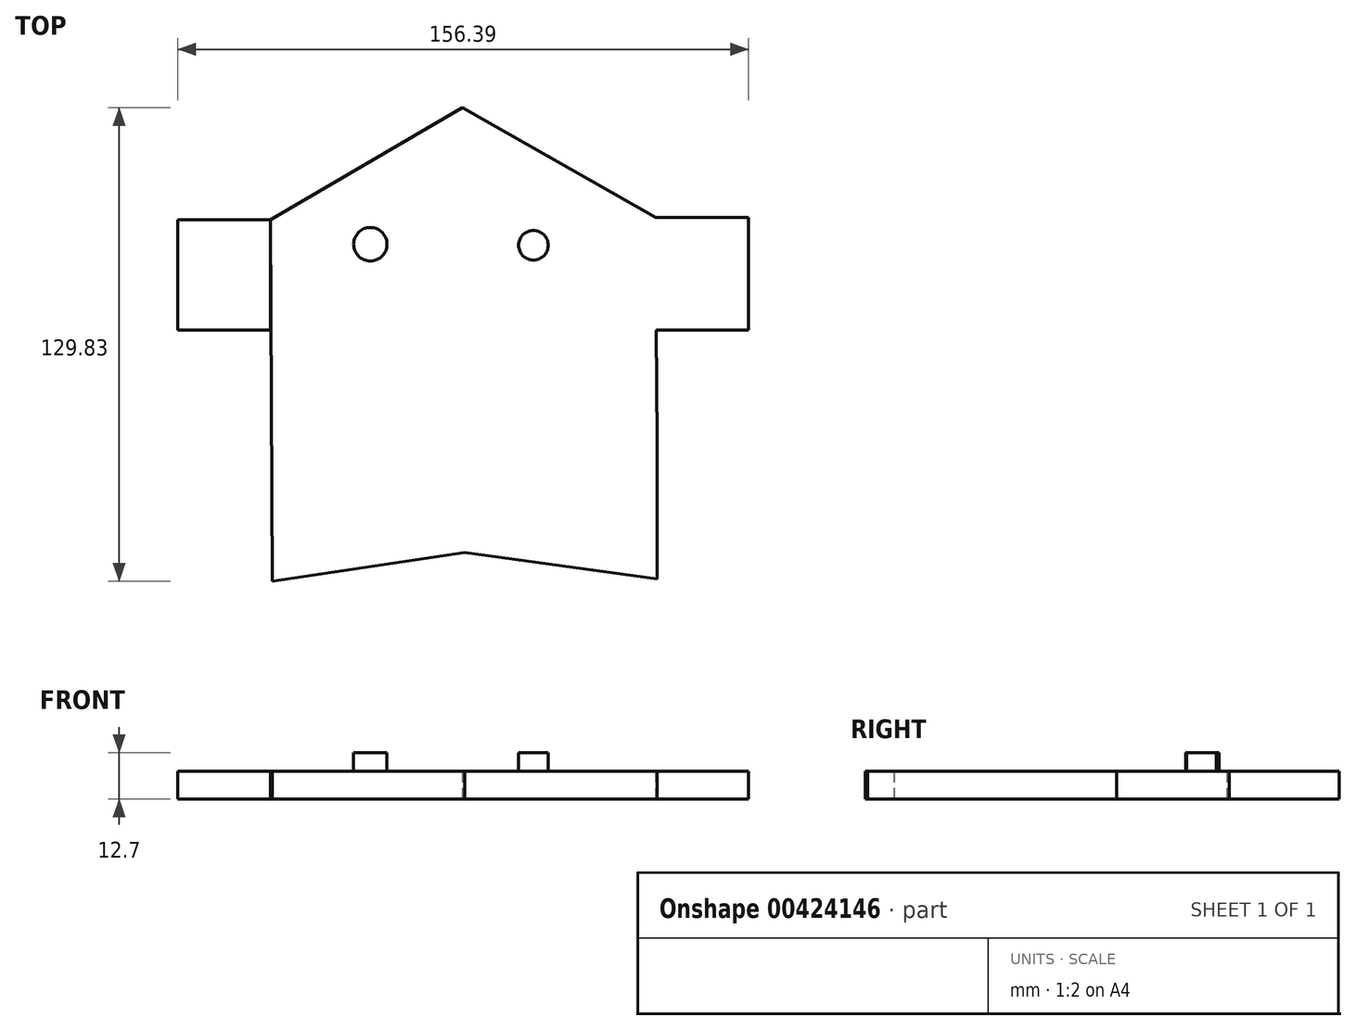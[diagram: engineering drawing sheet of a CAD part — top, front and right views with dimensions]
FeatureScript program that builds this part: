
annotation { "Feature Type Name" : "Feature", "Feature Type Description" : "" }
export const myFeature = defineFeature(function(context is Context, id is Id, definition is map)
    precondition{}
    {
        {
            var Q0;
            Q0=qCreatedBy(makeId("Top.planeOp"),FACE);
            var sketch = newSketch(context, id + "F0", { "sketchPlane" : qUnion([Q0])});
            skCircle(sketch, "E0.cCircle", {"center": v(0, 0) * mm, "radius": 52.8 * mm, "construction": true});
            skLineSegment(sketch, "E0.0", {"start": v(-52.96, 30.2) * mm, "end": v(-0.33, 60.96) * mm});
            skLineSegment(sketch, "E0.1", {"start": v(-0.33, 60.96) * mm, "end": v(52.63, 30.77) * mm});
            skLineSegment(sketch, "E0.2", {"start": v(52.63, 30.77) * mm, "end": v(52.96, -30.2) * mm});
            skLineSegment(sketch, "E0.3", {"start": v(52.96, -30.2) * mm, "end": v(0.33, -60.96) * mm});
            skLineSegment(sketch, "E0.4", {"start": v(0.33, -60.96) * mm, "end": v(-52.63, -30.77) * mm});
            skLineSegment(sketch, "E0.5", {"start": v(-52.63, -30.77) * mm, "end": v(-52.96, 30.2) * mm});
            skPoint(sketch, "E0.0.midPoint", {"position": v(-26.64, 45.58) * mm});
            skLineSegment(sketch, "E1", {"start": v(-52.63, -30.77) * mm, "end": v(-52.42, -68.87) * mm});
            skLineSegment(sketch, "E2", {"start": v(-52.42, -68.87) * mm, "end": v(0.33, -60.96) * mm});
            skLineSegment(sketch, "E3", {"start": v(52.96, -30.2) * mm, "end": v(52.96, -68.3) * mm});
            skLineSegment(sketch, "E4", {"start": v(52.96, -68.3) * mm, "end": v(0.33, -60.96) * mm});
            skLineSegment(sketch, "E5.bottom", {"start": v(-52.96, 30.2) * mm, "end": v(-78.36, 30.2) * mm});
            skLineSegment(sketch, "E5.top", {"start": v(-52.96, 0) * mm, "end": v(-78.36, 0) * mm});
            skLineSegment(sketch, "E5.left", {"start": v(-52.96, 30.2) * mm, "end": v(-52.96, 0) * mm});
            skLineSegment(sketch, "E5.right", {"start": v(-78.36, 30.2) * mm, "end": v(-78.36, 0) * mm});
            skLineSegment(sketch, "E6.bottom", {"start": v(52.63, 30.77) * mm, "end": v(78.03, 30.77) * mm});
            skLineSegment(sketch, "E6.top", {"start": v(52.63, 0) * mm, "end": v(78.03, 0) * mm});
            skLineSegment(sketch, "E6.left", {"start": v(52.63, 30.77) * mm, "end": v(52.63, 0) * mm});
            skLineSegment(sketch, "E6.right", {"start": v(78.03, 30.77) * mm, "end": v(78.03, 0) * mm});
            skSolve(sketch);
        }
        {
            var Q0;
            Q0=makeQuery(id+"F0.imprint","IMPRINT",FACE,{"disambiguationData":[TD([[makeQuery(id+"F0.imprint","IMPRINT",EDGE,{"derivedFrom":sQuery(id+"F0.wireOp",EDGE,"E0.3")}),1.0]])]});
            var Q1;
            {var subQ0=sQuery(id+"F0.wireOp",EDGE,"E6.bottom");Q1=makeQuery(id+"F0.imprint","IMPRINT",FACE,{"disambiguationData":[TD([[makeQuery(id+"F0.imprint","IMPRINT",EDGE,{"derivedFrom":subQ0}),-1.0]])]});}
            var Q2;
            Q2=makeQuery(id+"F0.imprint","IMPRINT",FACE,{"disambiguationData":[TD([[makeQuery(id+"F0.imprint","IMPRINT",EDGE,{"derivedFrom":sQuery(id+"F0.wireOp",EDGE,"E5.bottom")}),1.0]])]});
            var Q3;
            Q3=makeQuery(id+"F0.imprint","IMPRINT",FACE,{"disambiguationData":[TD([[makeQuery(id+"F0.imprint","IMPRINT",EDGE,{"derivedFrom":sQuery(id+"F0.wireOp",EDGE,"E0.4")}),1.0]])]});
            var Q4;
            Q4=makeQuery(id+"F0.imprint","IMPRINT",FACE,{"disambiguationData":[TD([[makeQuery(id+"F0.imprint","IMPRINT",EDGE,{"derivedFrom":sQuery(id+"F0.wireOp",EDGE,"E0.0")}),-1.0]])]});
            var Q5;
            {var subQ0=sQuery(id+"F0.wireOp",EDGE,"E6.left");Q5=makeQuery(id+"F0.imprint","IMPRINT",FACE,{"disambiguationData":[TD([[makeQuery(id+"F0.imprint","IMPRINT",EDGE,{"derivedFrom":subQ0}),1.0]])]});}
            extrude(context, id + "F1", {"entities" : qUnion([Q0, Q1, Q2, Q3, Q4, Q5]), "depth" : 7.62 * mm});
        }
        {
            var Q0;
            Q0=makeQuery(id+"F1.opExtrude","CAP_FACE",FACE,{"disambiguationData":[OSD([sQuery(id+"F0.wireOp",EDGE,"E0.0"),sQuery(id+"F0.wireOp",EDGE,"E0.1"),sQuery(id+"F0.wireOp",EDGE,"E0.2"),sQuery(id+"F0.wireOp",EDGE,"E0.5"),sQuery(id+"F0.wireOp",EDGE,"E1"),sQuery(id+"F0.wireOp",EDGE,"E2"),sQuery(id+"F0.wireOp",EDGE,"E3"),sQuery(id+"F0.wireOp",EDGE,"E4"),sQuery(id+"F0.wireOp",EDGE,"E6.bottom"),sQuery(id+"F0.wireOp",EDGE,"E6.top"),sQuery(id+"F0.wireOp",EDGE,"E6.right")])],"isStart":false});
            var sketch = newSketch(context, id + "F2", { "sketchPlane" : qUnion([Q0])});
            skCircle(sketch, "E7", {"center": v(-25.53, 23.71) * mm, "radius": 10.43 * mm});
            skCircle(sketch, "E8", {"center": v(18.85, 23.71) * mm, "radius": 10.43 * mm});
            skArc(sketch, "E9", {"start": v(-19.44, -6.97) * mm, "mid": v(-0.24, -17.82) * mm, "end": v(17.84, -5.2) * mm});
            skSolve(sketch);
        }
        {
            var Q0;
            Q0=sQuery(id+"F2.wireOp",EDGE,"E7");
            var Q1;
            Q1=sQuery(id+"F2.wireOp",EDGE,"E9");
            var Q2;
            Q2=sQuery(id+"F2.wireOp",EDGE,"E8");
            var Q3;
            Q3 = qConstructionFilter(qBodyType(qCreatedBy(id + "F6" ,EDGE), BodyType.WIRE), ConstructionObject.NO);
            extrude(context, id + "F3", {"bodyType" : ToolBodyType.SURFACE, "surfaceEntities" : qUnion([Q0, Q1, Q2, Q3]), "depth" : 5.08 * mm});
        }
        {
            var Q0;
            Q0=makeQuery(id+"F1.opExtrude","CAP_FACE",FACE,{"disambiguationData":[OSD([sQuery(id+"F0.wireOp",EDGE,"E0.0"),sQuery(id+"F0.wireOp",EDGE,"E0.1"),sQuery(id+"F0.wireOp",EDGE,"E0.2"),sQuery(id+"F0.wireOp",EDGE,"E0.5"),sQuery(id+"F0.wireOp",EDGE,"E1"),sQuery(id+"F0.wireOp",EDGE,"E2"),sQuery(id+"F0.wireOp",EDGE,"E3"),sQuery(id+"F0.wireOp",EDGE,"E4"),sQuery(id+"F0.wireOp",EDGE,"E6.bottom"),sQuery(id+"F0.wireOp",EDGE,"E6.top"),sQuery(id+"F0.wireOp",EDGE,"E6.right")])],"isStart":false});
            var sketch = newSketch(context, id + "F4", { "sketchPlane" : qUnion([Q0])});
            skCircle(sketch, "E10", {"center": v(-25.78, 23.46) * mm, "radius": 4.09 * mm});
            skCircle(sketch, "E11", {"center": v(19.1, 23.2) * mm, "radius": 4.06 * mm});
            skSolve(sketch);
        }
        {
            var Q0;
            Q0=makeQuery(id+"F4.imprint","IMPRINT",FACE,{"disambiguationData":[TD([[makeQuery(id+"F4.imprint","IMPRINT",EDGE,{"derivedFrom":sQuery(id+"F4.wireOp",EDGE,"E11")}),1.0]])]});
            extrude(context, id + "F5", {"entities" : qUnion([Q0]), "operationType" : NewBodyOperationType.ADD, "depth" : 5.08 * mm});
        }
        {
            var Q0;
            Q0=makeQuery(id+"F1.opExtrude","CAP_FACE",FACE,{"disambiguationData":[OSD([sQuery(id+"F0.wireOp",EDGE,"E0.0"),sQuery(id+"F0.wireOp",EDGE,"E0.1"),sQuery(id+"F0.wireOp",EDGE,"E0.2"),sQuery(id+"F0.wireOp",EDGE,"E0.5"),sQuery(id+"F0.wireOp",EDGE,"E1"),sQuery(id+"F0.wireOp",EDGE,"E2"),sQuery(id+"F0.wireOp",EDGE,"E3"),sQuery(id+"F0.wireOp",EDGE,"E4"),sQuery(id+"F0.wireOp",EDGE,"E6.bottom"),sQuery(id+"F0.wireOp",EDGE,"E6.top"),sQuery(id+"F0.wireOp",EDGE,"E6.right")])],"isStart":false});
            var sketch = newSketch(context, id + "F6", { "sketchPlane" : qUnion([Q0])});
            skCircle(sketch, "E12", {"center": v(-25.55, 23.5) * mm, "radius": 4.58 * mm});
            skSolve(sketch);
        }
        {
            var Q0;
            Q0 = qSketchRegion(id + "F6", true);
            extrude(context, id + "F7", {"entities" : qUnion([Q0]), "operationType" : NewBodyOperationType.ADD, "depth" : 5.08 * mm});
        }
    });
